# Revit family: 2093196
name_source: partatom
category: Lighting Fixtures
revit_build: Autodesk Revit 2018 (Build: 20170223_1515(x64)
units: mm (PartAtom-declared; Revit-internal decimal feet)

## family parameters
Cut with Voids When Loaded = No
Host = Face
Light Source = No
OmniClass Number = 23.80.70.00
OmniClass Title = Lighting
Part Type = Normal
Room Calculation Point = No
Round Connector Dimension = Use Diameter
Shared = No

## types (1)
- 2093196 MC2  90° CORNER L 4K DALI WHT OPAL
    Apparent Load = 10 VA
    Assembly Code = D5020200
    AssetType = Fixed
    ClassificationName = Uniclass2015
    ClassificationValue = EF_70_80
    Cost = 0 $
    Default Elevation = 1219 mm
    Description = MC2  90° HORIZNTL CORNER LEFT 4K DA WHT OPAL is an illuminated 90 degrees horizontal corner complimenting the Mini Continuum II continuous line of light. White RAL 9016, direct distribution, trimless detail for a seamless finish, suitable for recessed, semi-recessed, surface-mounted or suspended installation either horizontally or vertically, various accessories available, compact and minimalist design based on the Golden Mean, ideal for offices, meeting rooms, corridors, education facilities, museums and libraries, extruded aluminium body, diffuser: opal, colour temperature: 4000K neutral white, total system power: 10W, total fixture output: 980lm, luminaire efficacy: 98lm/W, LOR: 100%, colour rendering: Ra >80, LED Chromacity: 3 step MacAdam ellipse, lifespan: 66,000 hours L90B10, energy class: A++, A+, A, IR/UV free light source without heat radiation, operating voltage: 220-240V / 50-60Hz, drive current: 400mA, electronic driver, DALI dimmable, electrical protection: CLASS I, IP20, suitable for internal environment only
    DocumentationLiterature = http://www.sylvania-lighting.com
    DurationUnit = hours
    ElectricShockClassification = 98
    ExpectedLife = 50000
    Height = 86 mm
    IfcExportAs = Class I
    IfcExportType = IfcLightFixtureType
    ImpactProtectionIndex = IfcLightFixtureType
    IngressProtection = IfcLightFixtureType
    InputNominalFrequency = 4000
    InputVoltage = 0
    LampColourRenderingIndex = 16500
    LampColourTemperature = LED
    LampMacAdamStep = 80
    LampNominalLuminous = 4000 K
    Length = 340 mm  [stored 1.11549 ft]
    LightOutputRatio = LED
    LuminaireType = 0
    ManufacturerName = 98 lm/W
    Material = Feilo Sylvania
    Material_1_FEILO = <By Category>
    Material_2_FEILO = <By Category>
    Material_3_FEILO = <By Category>
    Material_4_FEILO = <By Category>
    Model = MC2  90° HORIZNTL CORNER LEFT 4K DA WHT OPAL
    ModelNumber = 2093196
    ModelReference = MC2  90° HORIZNTL CORNER LEFT 4K DA WHT OPAL
    Name = MC2  90° HORIZNTL CORNER LEFT 4K DA WHT OPAL
    NominalDepth = 0 mm  [stored 0 ft]
    NominalHeight = 0 mm  [stored 0 ft]
    NominalLength = 54 mm
    PowerConsumption = Lighting
    PowerFactor = 0
    Type Image = <None>
    TypeName = MC2  90° HORIZNTL CORNER LEFT 4K DA WHT OPAL
    URL = 0.86
    Voltage = 0 V
    WarrantyDescription = http://www.sylvania-lighting.com
    Width = 340 mm  [stored 1.11549 ft]

note: [stored X ft] marks values corroborated as IEEE doubles in the binary element streams (Revit-internal decimal feet)

## geometry (parser evidence)
native form markers: Sweep x6
no freeform markers — native parametric forms only
